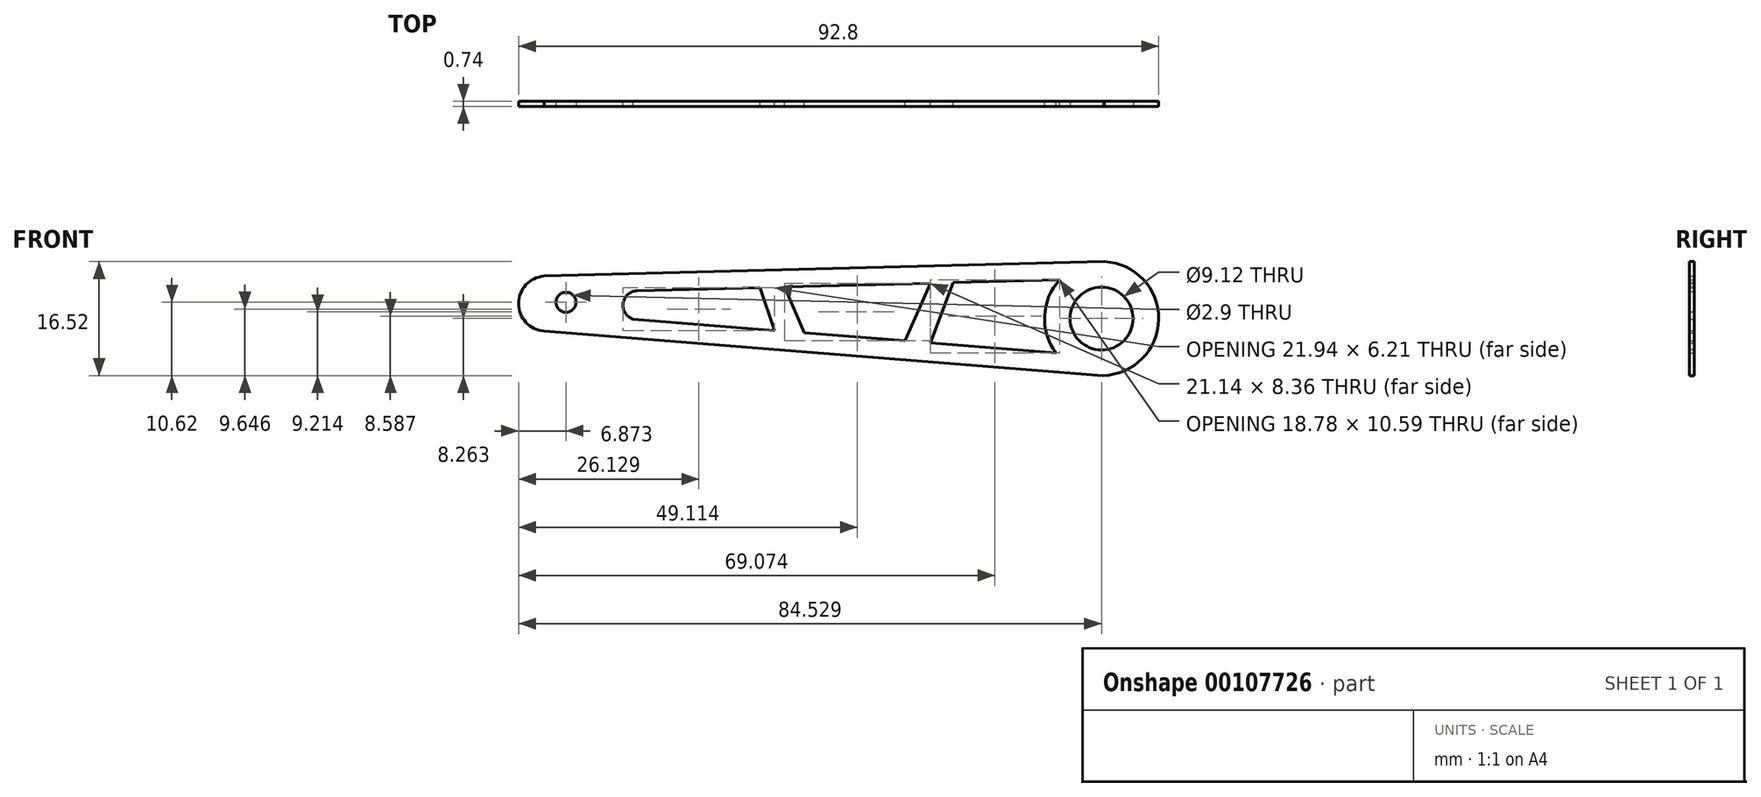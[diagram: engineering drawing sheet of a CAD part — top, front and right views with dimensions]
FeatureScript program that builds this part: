
annotation { "Feature Type Name" : "Feature", "Feature Type Description" : "" }
export const myFeature = defineFeature(function(context is Context, id is Id, definition is map)
    precondition{}
    {
        {
            var Q0;
            Q0=qCreatedBy(makeId("Front.planeOp"),FACE);
            var sketch = newSketch(context, id + "F0", { "sketchPlane" : qUnion([Q0])});
            skCircle(sketch, "E0", {"center": v(33.85, -2.36) * mm, "radius": 8.27 * mm});
            skLineSegment(sketch, "E1", {"start": v(34.25, 5.9) * mm, "end": v(-46.98, 3.8) * mm});
            skLineSegment(sketch, "E2", {"start": v(34.05, -10.62) * mm, "end": v(-47, -4.17) * mm});
            skArc(sketch, "E3", {"start": v(-46.98, 3.8) * mm, "mid": v(-50.68, -0.18) * mm, "end": v(-47, -4.17) * mm});
            skLineSegment(sketch, "E4", {"start": v(27.24, -7.33) * mm, "end": v(-34.08, -2.45) * mm});
            skLineSegment(sketch, "E5", {"start": v(27.78, 3.26) * mm, "end": v(-33.49, 1.67) * mm});
            skArc(sketch, "E6", {"start": v(-33.49, 1.67) * mm, "mid": v(-35.52, -0.14) * mm, "end": v(-34.08, -2.45) * mm});
            skLineSegment(sketch, "E7", {"start": v(9, -5.88) * mm, "end": v(12.33, 2.86) * mm});
            skLineSegment(sketch, "E8", {"start": v(5.33, -5.59) * mm, "end": v(9, 2.77) * mm});
            skLineSegment(sketch, "E9", {"start": v(-9.28, -4.42) * mm, "end": v(-12.14, 2.22) * mm});
            skLineSegment(sketch, "E10", {"start": v(-13.58, -4.08) * mm, "end": v(-15.68, 2.13) * mm});
            skSolve(sketch);
        }
        {
            var Q0;
            {var subQ21=sQuery(id+"F0.wireOp",EDGE,"E3");Q0=makeQuery(id+"F0.imprint","IMPRINT",FACE,{"disambiguationData":[TD([[makeQuery(id+"F0.imprint","IMPRINT",EDGE,{"derivedFrom":subQ21}),1.0]])]});}
            var Q1;
            {var subQ1=sQuery(id+"F0.wireOp",EDGE,"E0");var subQ7=makeQuery(id+"F0.imprint","INTERSECT",VERTEX,{"derivedFrom":[subQ1,sQuery(id+"F0.wireOp",EDGE,"E5")]});Q1=makeQuery(id+"F0.imprint","IMPRINT",FACE,{"disambiguationData":[TD([[makeQuery(id+"F0.imprint","IMPRINT",EDGE,{"disambiguationData":[TD([[subQ7,1.0]])],"derivedFrom":subQ1}),1.0]])]});}
            var Q2;
            {var subQ0=sQuery(id+"F0.wireOp",EDGE,"E7");Q2=makeQuery(id+"F0.imprint","IMPRINT",FACE,{"disambiguationData":[TD([[makeQuery(id+"F0.imprint","IMPRINT",EDGE,{"derivedFrom":subQ0}),1.0]])]});}
            var Q3;
            {var subQ0=sQuery(id+"F0.wireOp",EDGE,"E9");Q3=makeQuery(id+"F0.imprint","IMPRINT",FACE,{"disambiguationData":[TD([[makeQuery(id+"F0.imprint","IMPRINT",EDGE,{"derivedFrom":subQ0}),1.0]])]});}
            extrude(context, id + "F1", {"entities" : qUnion([Q0, Q1, Q2, Q3]), "depth" : 0.74 * mm});
        }
        {
            var Q0;
            Q0=makeQuery(id+"F1.opExtrude","CAP_FACE",FACE,{"disambiguationData":[OSD([sQuery(id+"F0.wireOp",EDGE,"E0"),sQuery(id+"F0.wireOp",EDGE,"E1"),sQuery(id+"F0.wireOp",EDGE,"E2"),sQuery(id+"F0.wireOp",EDGE,"E3"),sQuery(id+"F0.wireOp",EDGE,"E4"),sQuery(id+"F0.wireOp",EDGE,"E5"),sQuery(id+"F0.wireOp",EDGE,"E6"),sQuery(id+"F0.wireOp",EDGE,"E7"),sQuery(id+"F0.wireOp",EDGE,"E8"),sQuery(id+"F0.wireOp",EDGE,"E9"),sQuery(id+"F0.wireOp",EDGE,"E10")])],"isStart":false});
            var sketch = newSketch(context, id + "F2", { "sketchPlane" : qUnion([Q0])});
            skCircle(sketch, "E11", {"center": v(33.85, -2.36) * mm, "radius": 4.56 * mm});
            skSolve(sketch);
        }
        {
            var Q0;
            Q0=makeQuery(id+"F2.imprint","IMPRINT",FACE,{"disambiguationData":[TD([[makeQuery(id+"F2.imprint","IMPRINT",EDGE,{"derivedFrom":sQuery(id+"F2.wireOp",EDGE,"E11")}),1.0]])]});
            extrude(context, id + "F3", {"entities" : qUnion([Q0]), "operationType" : NewBodyOperationType.REMOVE, "oppositeDirection" : true, "depth" : 25.4 * mm});
        }
        {
            var Q0;
            Q0=makeQuery(id+"F1.opExtrude","CAP_FACE",FACE,{"disambiguationData":[OSD([sQuery(id+"F0.wireOp",EDGE,"E0"),sQuery(id+"F0.wireOp",EDGE,"E1"),sQuery(id+"F0.wireOp",EDGE,"E2"),sQuery(id+"F0.wireOp",EDGE,"E3"),sQuery(id+"F0.wireOp",EDGE,"E4"),sQuery(id+"F0.wireOp",EDGE,"E5"),sQuery(id+"F0.wireOp",EDGE,"E6"),sQuery(id+"F0.wireOp",EDGE,"E7"),sQuery(id+"F0.wireOp",EDGE,"E8"),sQuery(id+"F0.wireOp",EDGE,"E9"),sQuery(id+"F0.wireOp",EDGE,"E10")])],"isStart":false});
            var sketch = newSketch(context, id + "F4", { "sketchPlane" : qUnion([Q0])});
            skCircle(sketch, "E12", {"center": v(-43.8, 0) * mm, "radius": 1.45 * mm});
            skSolve(sketch);
        }
        {
            var Q0;
            Q0=makeQuery(id+"F4.imprint","IMPRINT",FACE,{"disambiguationData":[TD([[makeQuery(id+"F4.imprint","IMPRINT",EDGE,{"derivedFrom":sQuery(id+"F4.wireOp",EDGE,"E12")}),1.0]])]});
            extrude(context, id + "F5", {"entities" : qUnion([Q0]), "operationType" : NewBodyOperationType.REMOVE, "oppositeDirection" : true, "depth" : 25.4 * mm});
        }
    });
